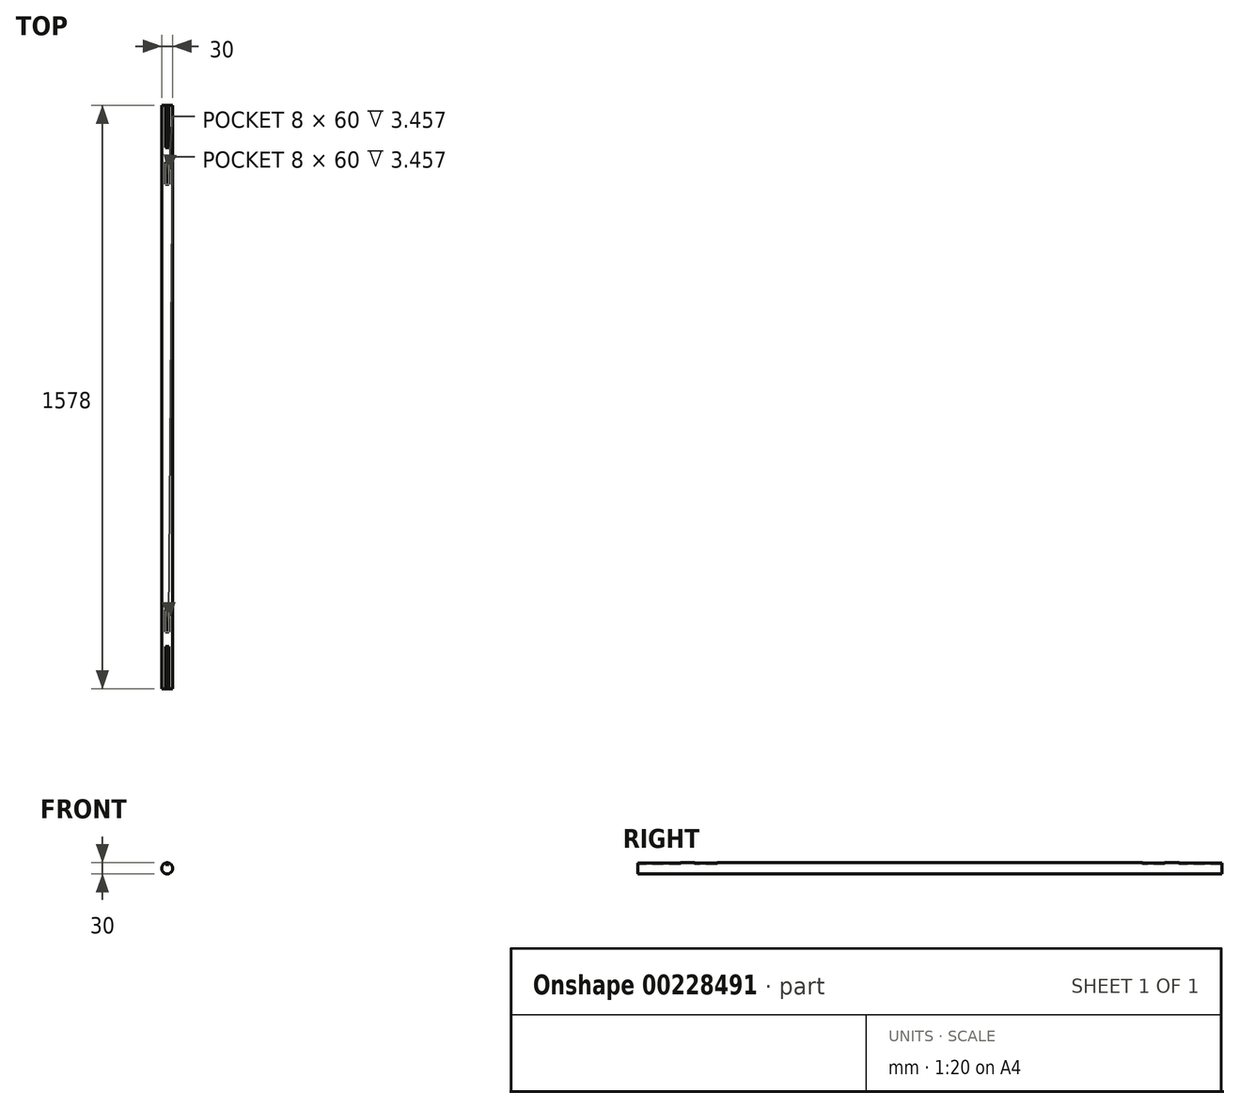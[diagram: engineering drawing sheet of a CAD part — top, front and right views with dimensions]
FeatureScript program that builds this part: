
annotation { "Feature Type Name" : "Feature", "Feature Type Description" : "" }
export const myFeature = defineFeature(function(context is Context, id is Id, definition is map)
    precondition{}
    {
        {
            var Q0;
            Q0=qCreatedBy(makeId("Front.planeOp"),FACE);
            var sketch = newSketch(context, id + "F0", { "sketchPlane" : qUnion([Q0])});
            skCircle(sketch, "E0", {"center": v(0, 0) * mm, "radius": 15 * mm});
            skSolve(sketch);
        }
        {
            var Q0;
            Q0=qSketchRegion(id+"F0",true);
            extrude(context, id + "F1", {"entities" : qUnion([Q0]), "depth" : 1578 * mm, "offsetDistance" : 25 * mm, "symmetric" : true});
        }
        {
            var Q0;
            Q0=qCreatedBy(makeId("Top.planeOp"),FACE);
            cPlane(context, id + "F2", {"entities" : qUnion([Q0]), "cplaneType" : CPlaneType.OFFSET, "offset" : 15 * mm, "width" : 150 * mm, "height" : 150 * mm});
        }
        {
            var Q0;
            Q0=qCreatedBy(id+"F2.planeOp",FACE);
            var sketch = newSketch(context, id + "F3", { "sketchPlane" : qUnion([Q0])});
            skLineSegment(sketch, "E1.bottom", {"start": v(-4, 789) * mm, "end": v(4, 789) * mm});
            skLineSegment(sketch, "E1.top", {"start": v(-4, 674) * mm, "end": v(4, 674) * mm});
            skLineSegment(sketch, "E1.left", {"start": v(-4, 789) * mm, "end": v(-4, 674) * mm});
            skLineSegment(sketch, "E1.right", {"start": v(4, 789) * mm, "end": v(4, 674) * mm});
            skLineSegment(sketch, "E2.bottom", {"start": v(-4, -575) * mm, "end": v(4, -575) * mm});
            skLineSegment(sketch, "E2.top", {"start": v(-4, -635) * mm, "end": v(4, -635) * mm});
            skLineSegment(sketch, "E2.left", {"start": v(-4, -575) * mm, "end": v(-4, -635) * mm});
            skLineSegment(sketch, "E2.right", {"start": v(4, -575) * mm, "end": v(4, -635) * mm});
            skLineSegment(sketch, "E3.bottom", {"start": v(-4, -674) * mm, "end": v(4, -674) * mm});
            skLineSegment(sketch, "E3.top", {"start": v(-4, -789) * mm, "end": v(4, -789) * mm});
            skLineSegment(sketch, "E3.left", {"start": v(-4, -674) * mm, "end": v(-4, -789) * mm});
            skLineSegment(sketch, "E3.right", {"start": v(4, -674) * mm, "end": v(4, -789) * mm});
            skLineSegment(sketch, "E4.bottom", {"start": v(-4, 635) * mm, "end": v(4, 635) * mm});
            skLineSegment(sketch, "E4.top", {"start": v(-4, 575) * mm, "end": v(4, 575) * mm});
            skLineSegment(sketch, "E4.left", {"start": v(-4, 635) * mm, "end": v(-4, 575) * mm});
            skLineSegment(sketch, "E4.right", {"start": v(4, 635) * mm, "end": v(4, 575) * mm});
            skSolve(sketch);
        }
        {
            var Q0;
            Q0=qSketchRegion(id+"F3",true);
            extrude(context, id + "F4", {"entities" : qUnion([Q0]), "operationType" : NewBodyOperationType.REMOVE, "oppositeDirection" : true, "depth" : 4 * mm, "offsetDistance" : 25 * mm});
        }
    });
